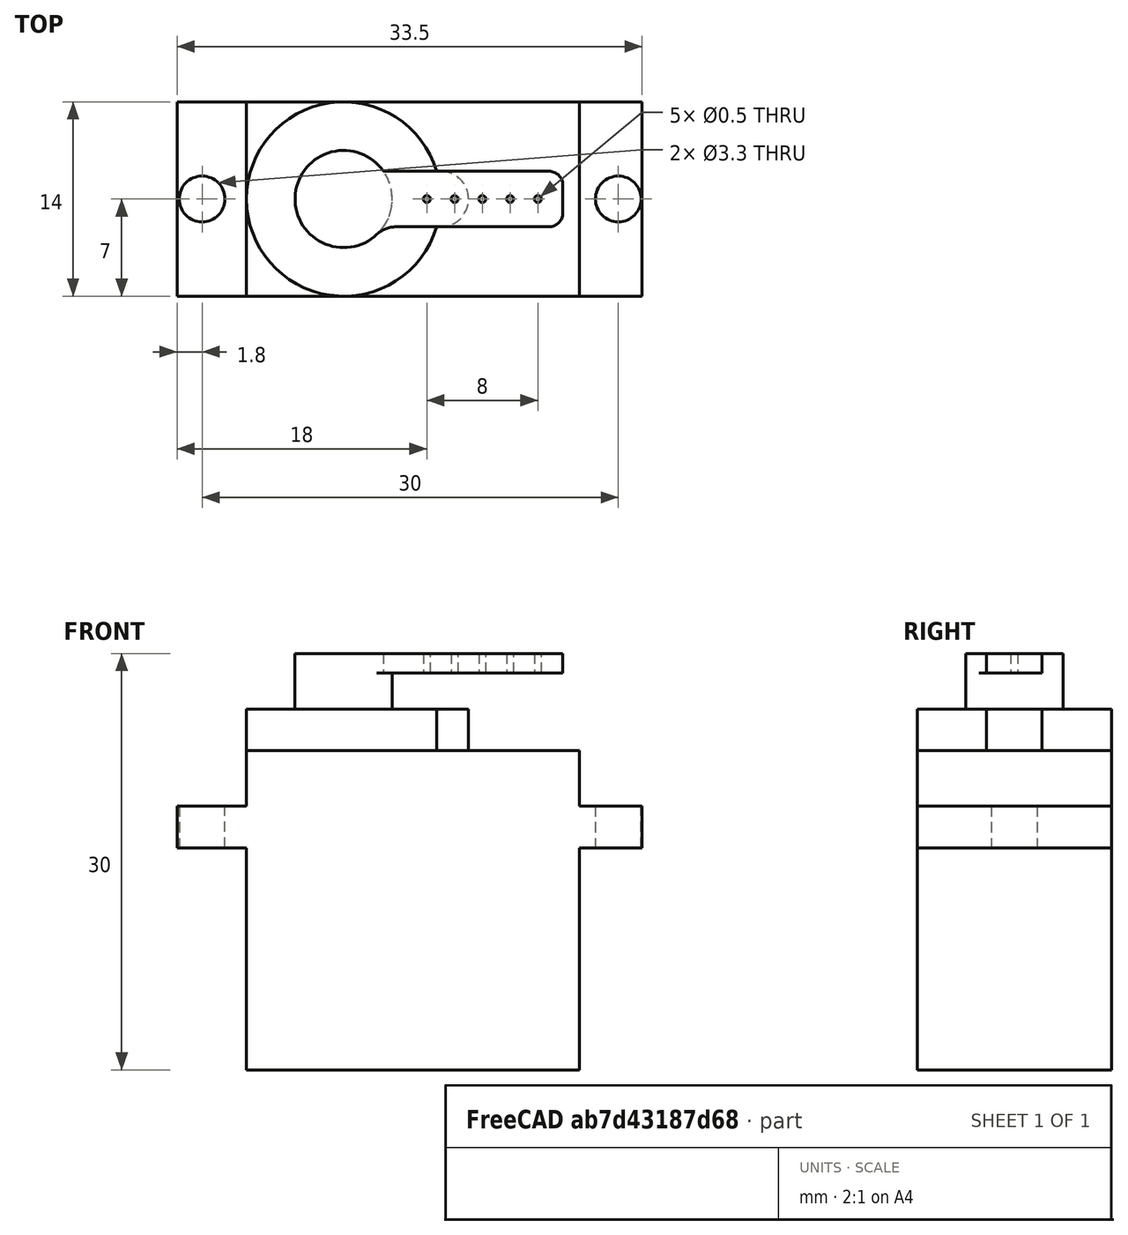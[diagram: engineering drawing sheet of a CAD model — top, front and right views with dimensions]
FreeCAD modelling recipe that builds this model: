
FCSTD DOCUMENT  (FreeCAD 0.20R29603 (Git))
Label: Servo
License: All rights reserved
LicenseURL: http://en.wikipedia.org/wiki/All_rights_reserved
objects: Part::Cylinder×10, Part::Cut×7, Part::MultiFuse×5, Part::Box×3, Part::Fillet×3
note: 28 computed .brp shape members not serialized (recipe doc carries the construction recipe); baked Part::Feature solids carry a one-line shape summary decoded from their .brp

FEATURE [Part::Box] Box092  label="Cubo092"
  AttacherType = Attacher::AttachEngine3D
  Height = 23
  Length = 24
  Width = 14
FEATURE [Part::Box] Box093  label="Cubo093"
  AttacherType = Attacher::AttachEngine3D
  Height = 3
  Length = 33.5
  Placement = pos=(-5,0,16) rot=(0,0,1;0rad)
  Width = 14
FEATURE [Part::Box] Box094  label="Cubo094"
  AttacherType = Attacher::AttachEngine3D
  Height = 1.4
  Length = 13
  Placement = pos=(9.8,5,28.6) rot=(0,0,1;0rad)
  Width = 4
FEATURE [Part::Cylinder] Cylinder061  label="Cilindro061"
  Angle = 360
  AttacherType = Attacher::AttachEngine3D
  FirstAngle = 0
  Height = 3
  Placement = pos=(7,7,23) rot=(0,0,1;0rad)
  Radius = 7
  SecondAngle = 0
FEATURE [Part::Cylinder] Cylinder062  label="Cilindro062"
  Angle = 360
  AttacherType = Attacher::AttachEngine3D
  FirstAngle = 0
  Height = 3
  Placement = pos=(14,7,23) rot=(0,0,1;0rad)
  Radius = 2
  SecondAngle = 0
FEATURE [Part::Cylinder] Cylinder063  label="Cilindro063"
  Angle = 360
  AttacherType = Attacher::AttachEngine3D
  FirstAngle = 0
  Height = 10
  Placement = pos=(-3.2,7,12) rot=(0,0,1;0rad)
  Radius = 1.65
  SecondAngle = 0
FEATURE [Part::Cylinder] Cylinder064  label="Cilindro064"
  Angle = 360
  AttacherType = Attacher::AttachEngine3D
  FirstAngle = 0
  Height = 10
  Placement = pos=(26.8,7,12) rot=(0,0,1;0rad)
  Radius = 1.65
  SecondAngle = 0
FEATURE [Part::Cylinder] Cylinder065  label="Cilindro065"
  Angle = 360
  AttacherType = Attacher::AttachEngine3D
  FirstAngle = 0
  Height = 4
  Placement = pos=(7,7,26) rot=(0,0,1;0rad)
  Radius = 3.5
  SecondAngle = 0
FEATURE [Part::Cylinder] Cylinder066  label="Cilindro066"
  Angle = 360
  AttacherType = Attacher::AttachEngine3D
  FirstAngle = 0
  Height = 10
  Placement = pos=(21,7,25) rot=(0,0,1;0rad)
  Radius = 0.25
  SecondAngle = 0
FEATURE [Part::Cylinder] Cylinder067  label="Cilindro067"
  Angle = 360
  AttacherType = Attacher::AttachEngine3D
  FirstAngle = 0
  Height = 10
  Placement = pos=(19,7,25) rot=(0,0,1;0rad)
  Radius = 0.25
  SecondAngle = 0
FEATURE [Part::Cylinder] Cylinder068  label="Cilindro068"
  Angle = 360
  AttacherType = Attacher::AttachEngine3D
  FirstAngle = 0
  Height = 10
  Placement = pos=(17,7,25) rot=(0,0,1;0rad)
  Radius = 0.25
  SecondAngle = 0
FEATURE [Part::Cylinder] Cylinder069  label="Cilindro069"
  Angle = 360
  AttacherType = Attacher::AttachEngine3D
  FirstAngle = 0
  Height = 10
  Placement = pos=(15,7,27) rot=(0,0,1;0rad)
  Radius = 0.25
  SecondAngle = 0
FEATURE [Part::Cylinder] Cylinder070  label="Cilindro070"
  Angle = 360
  AttacherType = Attacher::AttachEngine3D
  FirstAngle = 0
  Height = 10
  Placement = pos=(13,7,27) rot=(0,0,1;0rad)
  Radius = 0.25
  SecondAngle = 0
FEATURE [Part::MultiFuse] Fusion064
  Shapes = -> [Cylinder061,Cylinder062]
FEATURE [Part::MultiFuse] Fusion065
  Shapes = -> [Box092,Fusion064]
FEATURE [Part::MultiFuse] Fusion066
  Shapes = -> [Fusion065,Box093]
FEATURE [Part::Cut] Cut086
  Base = -> Fusion066
  Tool = -> Cylinder063
FEATURE [Part::Cut] Cut087  label="Servo"
  Base = -> Cut086
  Tool = -> Cylinder064
FEATURE [Part::MultiFuse] Fusion067
  Shapes = -> [Cylinder065,Box094]
FEATURE [Part::Fillet] Fillet027
  Base = -> Fusion067
  Edges = 1 edges r=2: [Edge4]
FEATURE [Part::Fillet] Fillet030
  Base = -> Fillet027
  Edges = 1 edges r=1: [Edge25]
FEATURE [Part::Fillet] Fillet031
  Base = -> Fillet030
  Edges = 1 edges r=1: [Edge17]
FEATURE [Part::MultiFuse] Fusion068
  Shapes = -> [Cut087,Fillet031]
FEATURE [Part::Cut] Cut088
  Base = -> Fusion068
  Tool = -> Cylinder066
FEATURE [Part::Cut] Cut089
  Base = -> Cut088
  Tool = -> Cylinder070
FEATURE [Part::Cut] Cut090
  Base = -> Cut089
  Tool = -> Cylinder069
FEATURE [Part::Cut] Cut091
  Base = -> Cut090
  Tool = -> Cylinder068
FEATURE [Part::Cut] Cut092  label="Servo006"
  Base = -> Cut091
  Placement = pos=(-12,27,-6) rot=(0,0,1;0rad)
  Tool = -> Cylinder067
